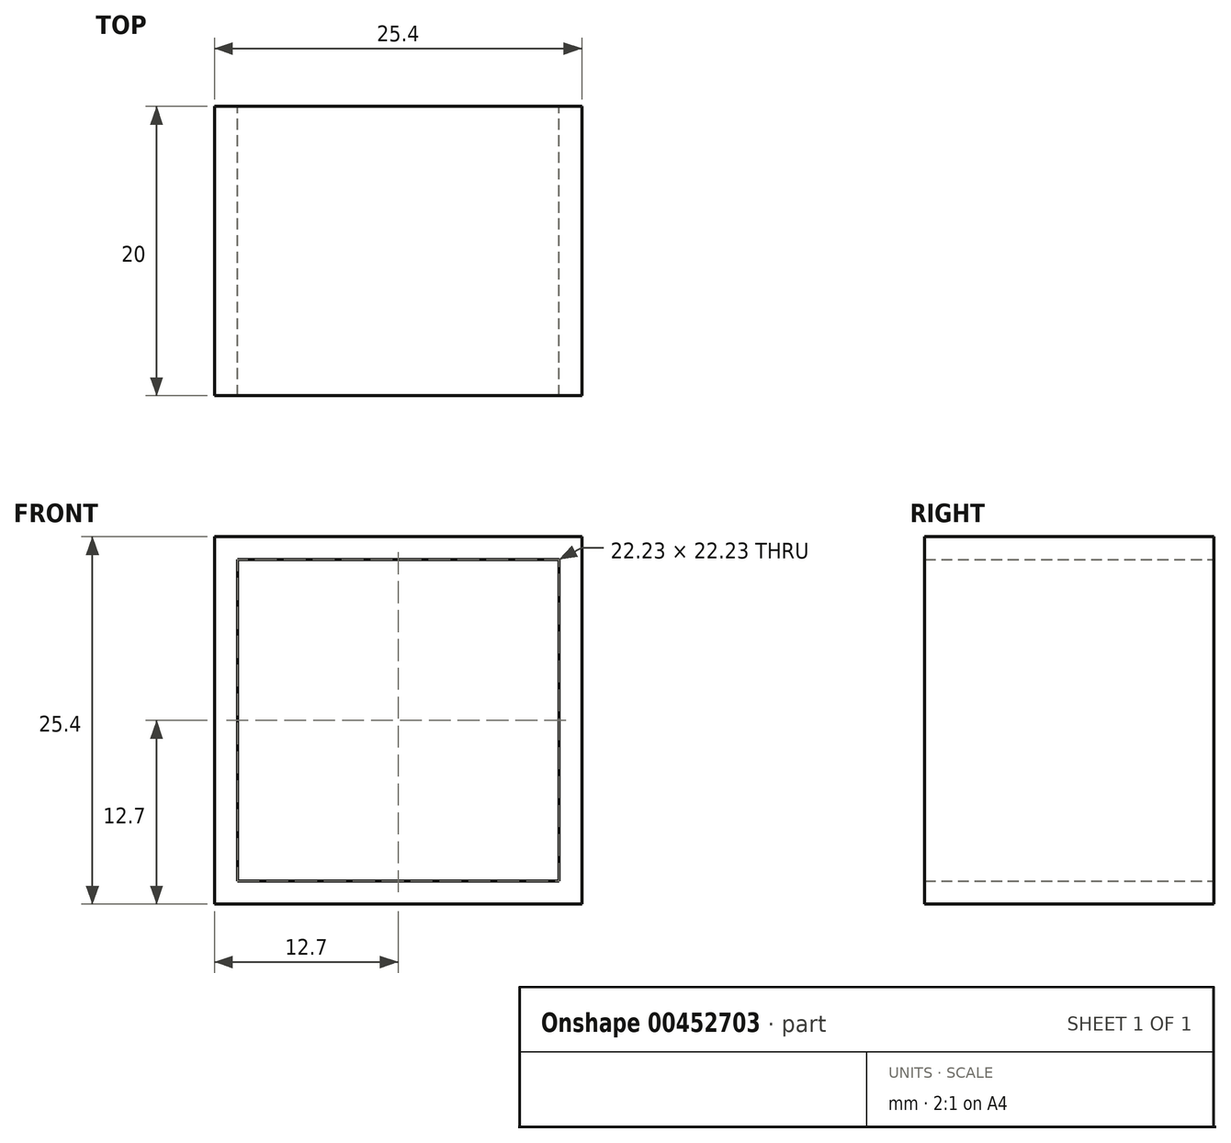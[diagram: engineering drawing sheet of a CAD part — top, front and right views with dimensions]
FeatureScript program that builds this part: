
annotation { "Feature Type Name" : "Feature", "Feature Type Description" : "" }
export const myFeature = defineFeature(function(context is Context, id is Id, definition is map)
    precondition{}
    {
        {
            assignVariable(context, id + "F0", {"name" : "XL", "anyValue" : 20});
        }
        {
            var Q0;
            Q0=qCreatedBy(makeId("Front.planeOp"),FACE);
            var sketch = newSketch(context, id + "F1", { "sketchPlane" : qUnion([Q0])});
            skLineSegment(sketch, "E0.bottom", {"start": v(-12.7, 12.7) * mm, "end": v(12.7, 12.7) * mm});
            skLineSegment(sketch, "E0.top", {"start": v(-12.7, -12.7) * mm, "end": v(12.7, -12.7) * mm});
            skLineSegment(sketch, "E0.left", {"start": v(-12.7, 12.7) * mm, "end": v(-12.7, -12.7) * mm});
            skLineSegment(sketch, "E0.right", {"start": v(12.7, 12.7) * mm, "end": v(12.7, -12.7) * mm});
            skPoint(sketch, "E0.middle", {"position": v(0, 0) * mm});
            skLineSegment(sketch, "E1.bottom", {"start": v(-11.11, 11.11) * mm, "end": v(11.11, 11.11) * mm});
            skLineSegment(sketch, "E1.top", {"start": v(-11.11, -11.11) * mm, "end": v(11.11, -11.11) * mm});
            skLineSegment(sketch, "E1.left", {"start": v(-11.11, 11.11) * mm, "end": v(-11.11, -11.11) * mm});
            skLineSegment(sketch, "E1.right", {"start": v(11.11, 11.11) * mm, "end": v(11.11, -11.11) * mm});
            skSolve(sketch);
        }
        {
            var Q0;
            Q0=makeQuery(id+"F1.imprint","IMPRINT",FACE,{"disambiguationData":[TD([[makeQuery(id+"F1.imprint","IMPRINT",EDGE,{"derivedFrom":sQuery(id+"F1.wireOp",EDGE,"E0.bottom")}),-1.0]])]});
            extrude(context, id + "F2", {"entities" : qUnion([Q0]), "depth" : (getVariable(context, 'XL')) * mm, "offsetDistance" : 25.4 * mm});
        }
    });
